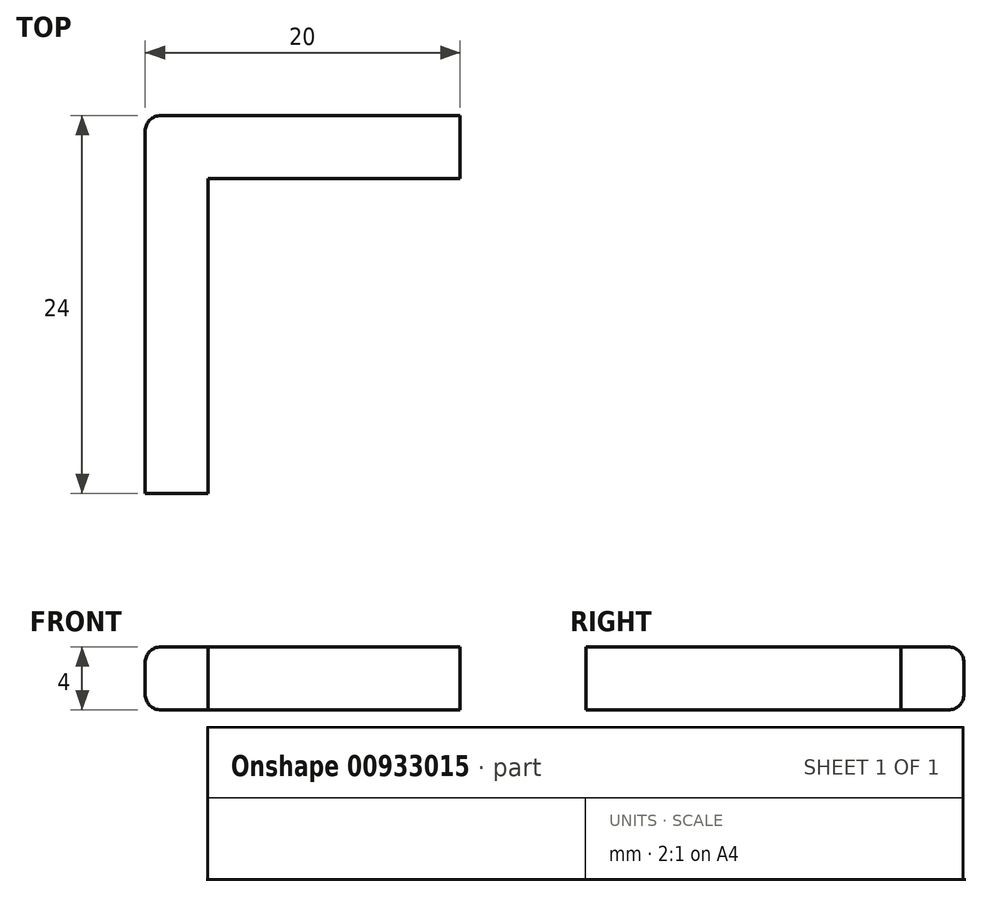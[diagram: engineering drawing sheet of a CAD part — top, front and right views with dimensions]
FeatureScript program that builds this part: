
annotation { "Feature Type Name" : "Feature", "Feature Type Description" : "" }
export const myFeature = defineFeature(function(context is Context, id is Id, definition is map)
    precondition{}
    {
        {
            var Q0;
            Q0=qCreatedBy(makeId("Top.planeOp"),FACE);
            var sketch = newSketch(context, id + "F0", { "sketchPlane" : qUnion([Q0])});
            skLineSegment(sketch, "E0.bottom", {"start": v(10, 2) * mm, "end": v(-10, 2) * mm});
            skLineSegment(sketch, "E0.top", {"start": v(10, -2) * mm, "end": v(-10, -2) * mm});
            skLineSegment(sketch, "E0.left", {"start": v(10, 2) * mm, "end": v(10, -2) * mm});
            skLineSegment(sketch, "E0.right", {"start": v(-10, 2) * mm, "end": v(-10, -2) * mm});
            skPoint(sketch, "E0.middle", {"position": v(0, 0) * mm});
            skSolve(sketch);
        }
        {
            var Q0;
            Q0=makeQuery(id+"F0.imprint","IMPRINT",FACE,{"disambiguationData":[TD([[makeQuery(id+"F0.imprint","IMPRINT",EDGE,{"derivedFrom":sQuery(id+"F0.wireOp",EDGE,"E0.bottom")}),1.0]])]});
            extrude(context, id + "F1", {"entities" : qUnion([Q0]), "depth" : 4 * mm, "offsetDistance" : 25 * mm});
        }
        {
            var Q0;
            Q0=makeQuery(id+"F1.opExtrude","SWEPT_FACE",FACE,{"disambiguationData":[OSD([sQuery(id+"F0.wireOp",EDGE,"E0.top")])]});
            var sketch = newSketch(context, id + "F2", { "sketchPlane" : qUnion([Q0])});
            skLineSegment(sketch, "E1", {"start": v(-10, 4) * mm, "end": v(-10, 0) * mm});
            skLineSegment(sketch, "E2", {"start": v(-10, 0) * mm, "end": v(-6, 0) * mm});
            skLineSegment(sketch, "E3", {"start": v(-6, 0) * mm, "end": v(-6, 4) * mm});
            skLineSegment(sketch, "E4", {"start": v(-6, 4) * mm, "end": v(-10, 4) * mm});
            skSolve(sketch);
        }
        {
            var Q0;
            Q0=makeQuery(id+"F2.imprint","IMPRINT",FACE,{"disambiguationData":[TD([[makeQuery(id+"F2.imprint","IMPRINT",EDGE,{"derivedFrom":sQuery(id+"F2.wireOp",EDGE,"E1")}),1.0]])]});
            extrude(context, id + "F3", {"entities" : qUnion([Q0]), "operationType" : NewBodyOperationType.ADD, "depth" : 20 * mm, "offsetDistance" : 25 * mm});
        }
        {
            var Q0;
            Q0=makeQuery(id+"F3.boolean.opBoolean","MERGE",EDGE,{"derivedFrom":[makeQuery(id+"F1.opExtrude","CAP_EDGE",EDGE,{"disambiguationData":[OSD([sQuery(id+"F0.wireOp",EDGE,"E0.right")])],"isStart":false}),makeQuery(id+"F3.opExtrude","SWEPT_EDGE",EDGE,{"disambiguationData":[OSD([sQuery(id+"F2.wireOp",EDGE,"E1"),sQuery(id+"F2.wireOp",EDGE,"E4")])]})]});
            fillet(context, id + "F4", {"entities" : qUnion([Q0]), "radius" : 1 * mm, "tangentPropagation" : true, "allowEdgeOverflow" : false});
        }
        {
            var Q0;
            Q0=makeQuery(id+"F3.boolean.opBoolean","MERGE",EDGE,{"derivedFrom":[makeQuery(id+"F1.opExtrude","CAP_EDGE",EDGE,{"disambiguationData":[OSD([sQuery(id+"F0.wireOp",EDGE,"E0.right")])],"isStart":true}),makeQuery(id+"F3.opExtrude","SWEPT_EDGE",EDGE,{"disambiguationData":[OSD([sQuery(id+"F2.wireOp",EDGE,"E1"),sQuery(id+"F2.wireOp",EDGE,"E2")])]})]});
            fillet(context, id + "F5", {"entities" : qUnion([Q0]), "radius" : 1 * mm, "tangentPropagation" : true, "allowEdgeOverflow" : false});
        }
        {
            var Q0;
            Q0=makeQuery(id+"F1.opExtrude","CAP_EDGE",EDGE,{"disambiguationData":[OSD([sQuery(id+"F0.wireOp",EDGE,"E0.bottom")])],"isStart":false});
            var Q1;
            Q1=makeQuery(id+"F1.opExtrude","CAP_EDGE",EDGE,{"disambiguationData":[OSD([sQuery(id+"F0.wireOp",EDGE,"E0.bottom")])],"isStart":true});
            fillet(context, id + "F6", {"entities" : qUnion([Q0, Q1]), "radius" : 1 * mm, "tangentPropagation" : true, "allowEdgeOverflow" : false});
        }
    });
